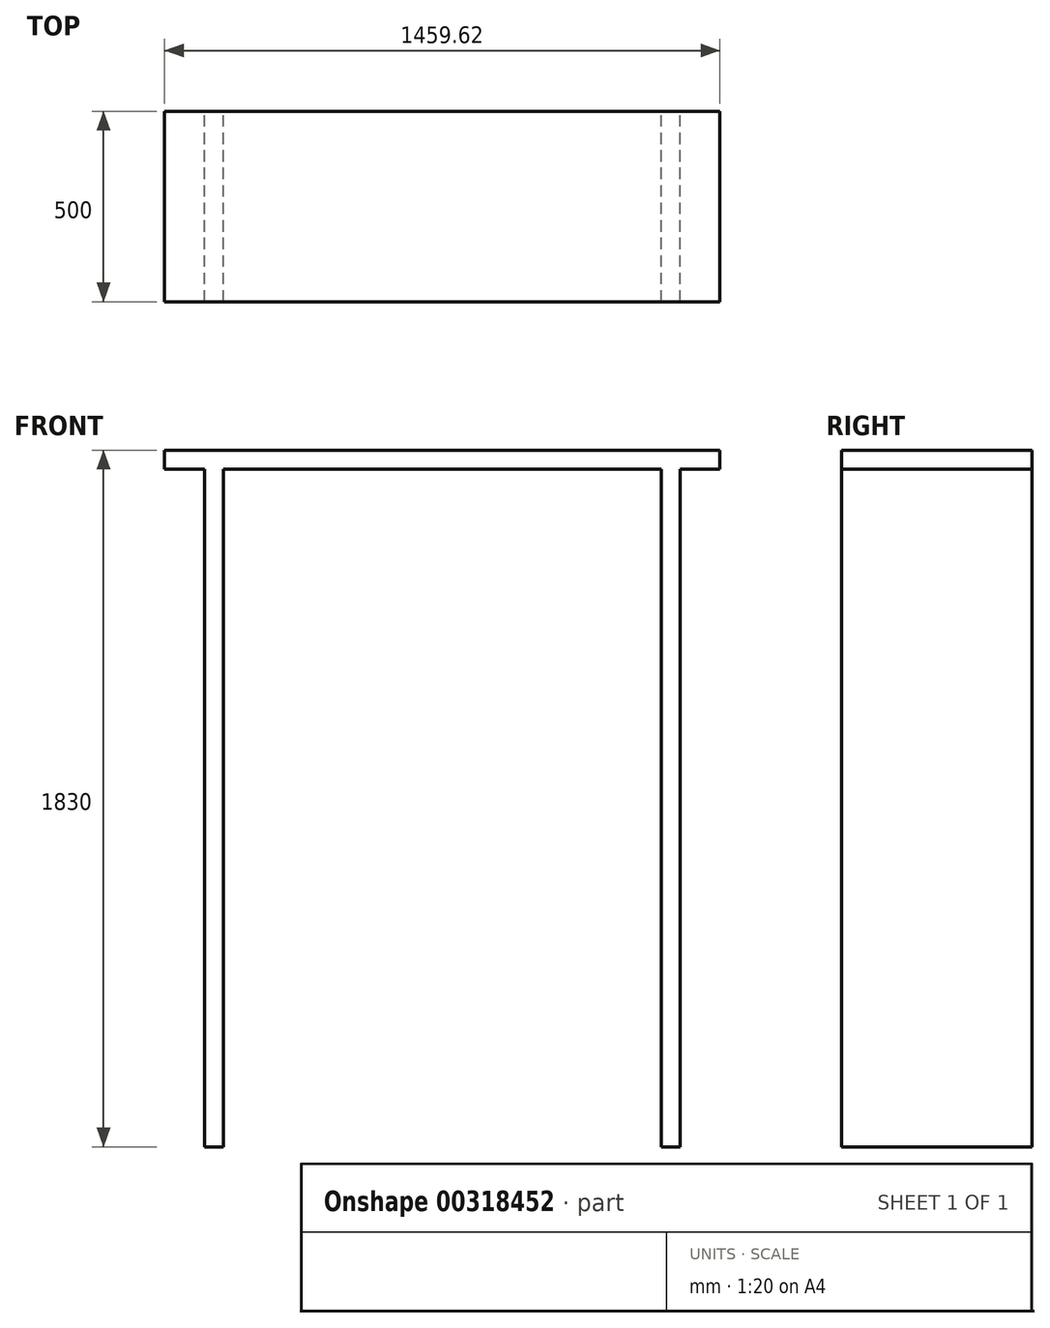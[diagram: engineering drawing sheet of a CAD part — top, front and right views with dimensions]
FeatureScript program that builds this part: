
annotation { "Feature Type Name" : "Feature", "Feature Type Description" : "" }
export const myFeature = defineFeature(function(context is Context, id is Id, definition is map)
    precondition{}
    {
        {
            var Q0;
            Q0=qCreatedBy(makeId("Front.planeOp"),FACE);
            var sketch = newSketch(context, id + "F0", { "sketchPlane" : qUnion([Q0])});
            skLineSegment(sketch, "E0.bottom", {"start": v(25, -890) * mm, "end": v(-25, -890) * mm});
            skLineSegment(sketch, "E0.top", {"start": v(25, 890) * mm, "end": v(-25, 890) * mm});
            skLineSegment(sketch, "E0.left", {"start": v(25, -890) * mm, "end": v(25, 890) * mm});
            skLineSegment(sketch, "E0.right", {"start": v(-25, -890) * mm, "end": v(-25, 890) * mm});
            skPoint(sketch, "E0.middle", {"position": v(0, 0) * mm});
            skLineSegment(sketch, "E1", {"start": v(600, 890) * mm, "end": v(600, -899.12) * mm, "construction": true});
            skLineSegment(sketch, "E2.MirrorCS", {"start": v(1175, -890) * mm, "end": v(1175, 890) * mm});
            skLineSegment(sketch, "E3.MirrorCS", {"start": v(1225, -890) * mm, "end": v(1225, 890) * mm});
            skLineSegment(sketch, "E4.MirrorCS", {"start": v(1175, -890) * mm, "end": v(1225, -890) * mm});
            skLineSegment(sketch, "E5.MirrorCS", {"start": v(1175, 890) * mm, "end": v(1225, 890) * mm});
            skLineSegment(sketch, "E6.bottom", {"start": v(1329.81, 940) * mm, "end": v(-129.81, 940) * mm});
            skLineSegment(sketch, "E6.top", {"start": v(1329.81, 890) * mm, "end": v(-129.81, 890) * mm});
            skLineSegment(sketch, "E6.left", {"start": v(1329.81, 940) * mm, "end": v(1329.81, 890) * mm});
            skLineSegment(sketch, "E6.right", {"start": v(-129.81, 940) * mm, "end": v(-129.81, 890) * mm});
            skPoint(sketch, "E6.middle", {"position": v(600, 915) * mm});
            skSolve(sketch);
        }
        {
            var Q0;
            Q0=makeQuery(id+"F0.imprint","IMPRINT",FACE,{"disambiguationData":[TD([[makeQuery(id+"F0.imprint","IMPRINT",EDGE,{"derivedFrom":sQuery(id+"F0.wireOp",EDGE,"E0.bottom")}),-1.0]])]});
            var Q1;
            Q1=makeQuery(id+"F0.imprint","IMPRINT",FACE,{"disambiguationData":[TD([[makeQuery(id+"F0.imprint","IMPRINT",EDGE,{"derivedFrom":sQuery(id+"F0.wireOp",EDGE,"E6.bottom")}),1.0]])]});
            var Q2;
            {var subQ0=sQuery(id+"F0.wireOp",EDGE,"E2.MirrorCS");Q2=makeQuery(id+"F0.imprint","IMPRINT",FACE,{"disambiguationData":[TD([[makeQuery(id+"F0.imprint","IMPRINT",EDGE,{"derivedFrom":subQ0}),-1.0]])]});}
            extrude(context, id + "F1", {"entities" : qUnion([Q0, Q1, Q2]), "depth" : 500 * mm});
        }
    });
